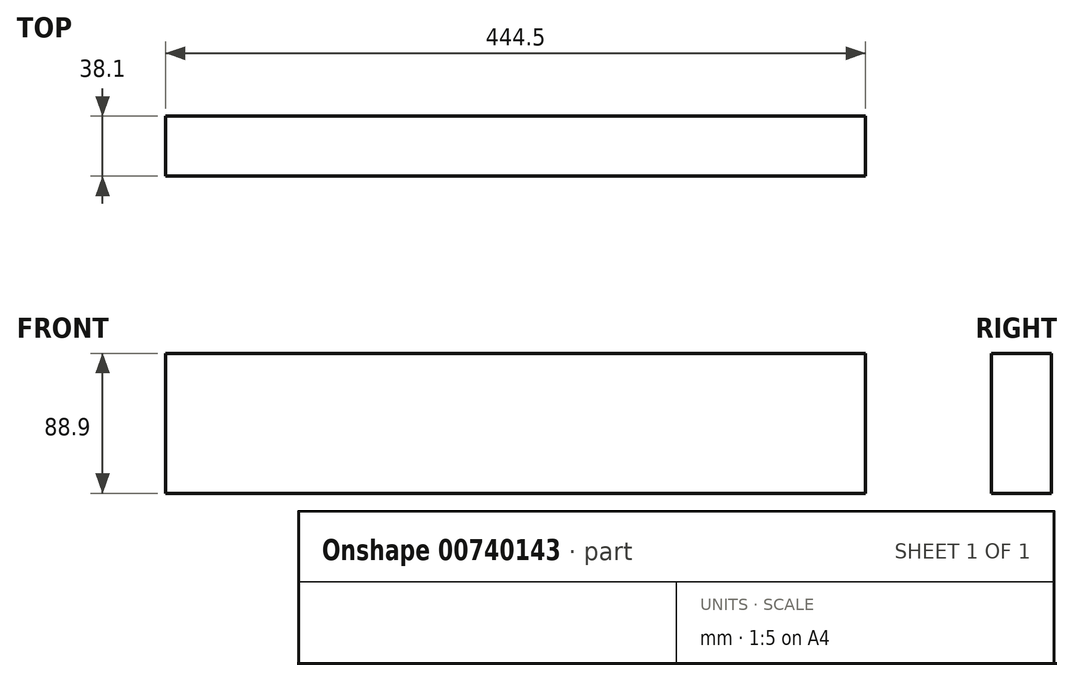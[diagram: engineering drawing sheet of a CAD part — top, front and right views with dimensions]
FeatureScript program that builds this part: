
annotation { "Feature Type Name" : "Feature", "Feature Type Description" : "" }
export const myFeature = defineFeature(function(context is Context, id is Id, definition is map)
    precondition{}
    {
        {
            var Q0;
            Q0=qCreatedBy(makeId("Right.planeOp"),FACE);
            var sketch = newSketch(context, id + "F0", { "sketchPlane" : qUnion([Q0])});
            skLineSegment(sketch, "E0.bottom", {"start": v(-79.68, 85.36) * mm, "end": v(-41.58, 85.36) * mm});
            skLineSegment(sketch, "E0.top", {"start": v(-79.68, -3.54) * mm, "end": v(-41.58, -3.54) * mm});
            skLineSegment(sketch, "E0.left", {"start": v(-79.68, 85.36) * mm, "end": v(-79.68, -3.54) * mm});
            skLineSegment(sketch, "E0.right", {"start": v(-41.58, 85.36) * mm, "end": v(-41.58, -3.54) * mm});
            skSolve(sketch);
        }
        {
            var Q0;
            Q0=makeQuery(id+"F0.imprint","IMPRINT",FACE,{"disambiguationData":[TD([[makeQuery(id+"F0.imprint","IMPRINT",EDGE,{"derivedFrom":sQuery(id+"F0.wireOp",EDGE,"E0.bottom")}),-1.0]])]});
            extrude(context, id + "F1", {"entities" : qUnion([Q0]), "depth" : 444.5 * mm, "offsetDistance" : 25.4 * mm});
        }
    });
